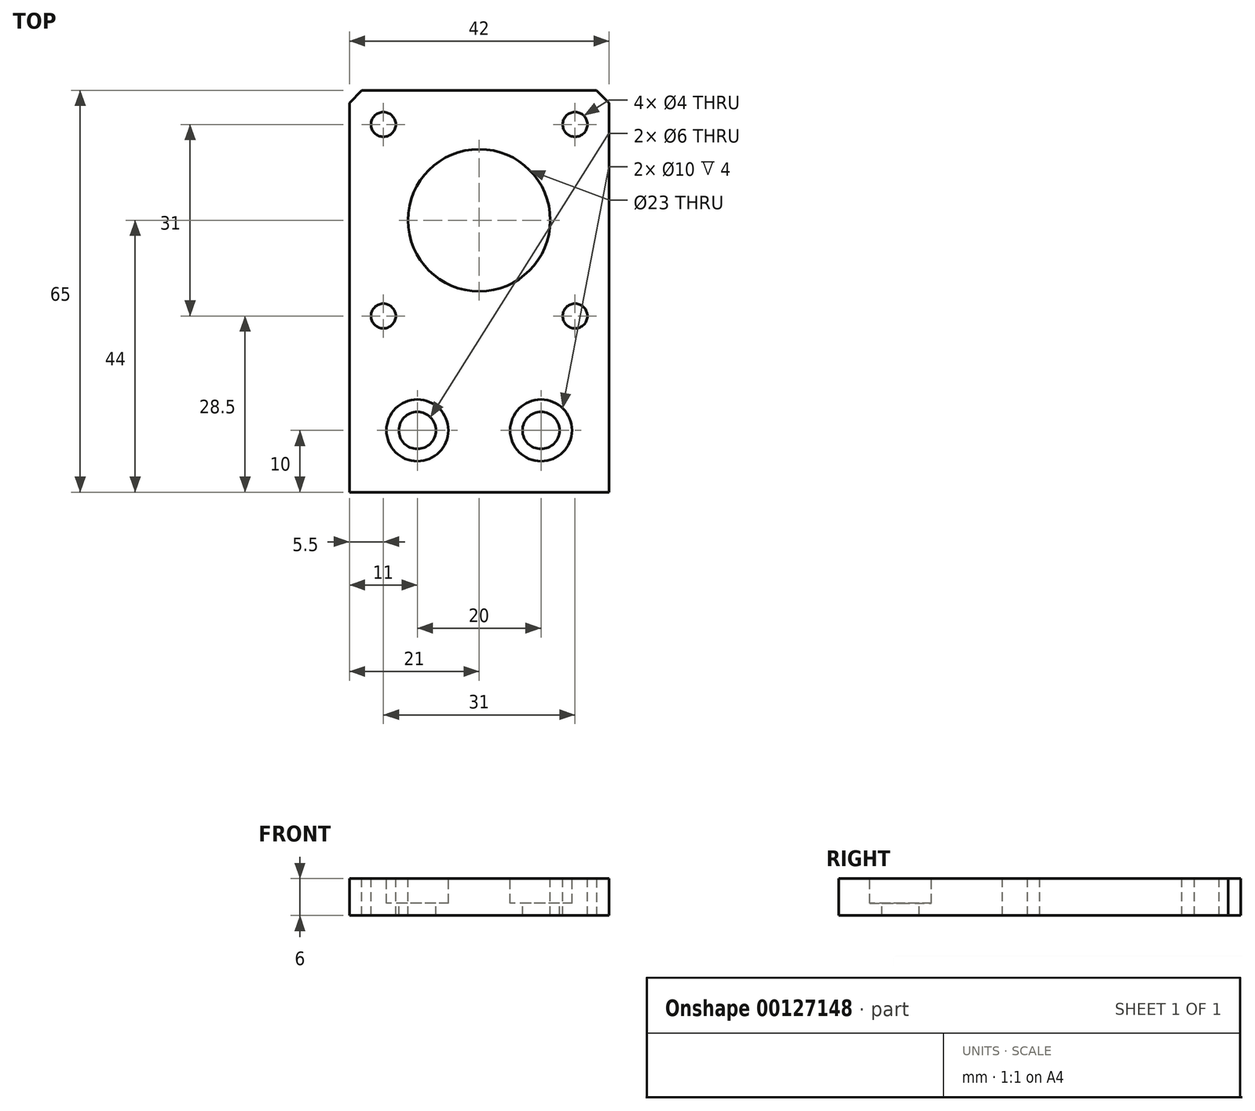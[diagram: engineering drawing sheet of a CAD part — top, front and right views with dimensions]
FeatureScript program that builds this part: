
annotation { "Feature Type Name" : "Feature", "Feature Type Description" : "" }
export const myFeature = defineFeature(function(context is Context, id is Id, definition is map)
    precondition{}
    {
        {
            var Q0;
            Q0=qCreatedBy(makeId("Top.planeOp"),FACE);
            var sketch = newSketch(context, id + "F0", { "sketchPlane" : qUnion([Q0])});
            skLineSegment(sketch, "E0.bottom", {"start": v(21, 21) * mm, "end": v(-21, 21) * mm});
            skLineSegment(sketch, "E0.top", {"start": v(21, -21) * mm, "end": v(-21, -21) * mm});
            skLineSegment(sketch, "E0.left", {"start": v(21, 21) * mm, "end": v(21, -21) * mm});
            skLineSegment(sketch, "E0.right", {"start": v(-21, 21) * mm, "end": v(-21, -21) * mm});
            skPoint(sketch, "E0.middle", {"position": v(0, 0) * mm});
            skSolve(sketch);
        }
        {
            var Q0;
            Q0=makeQuery(id+"F0.imprint","IMPRINT",FACE,{"disambiguationData":[TD([[makeQuery(id+"F0.imprint","IMPRINT",EDGE,{"derivedFrom":sQuery(id+"F0.wireOp",EDGE,"E0.bottom")}),1.0]])]});
            extrude(context, id + "F1", {"entities" : qUnion([Q0]), "depth" : 4 * mm});
        }
        {
            var Q0;
            Q0=makeQuery(id+"F1.opExtrude","CAP_FACE",FACE,{"disambiguationData":[OSD([sQuery(id+"F0.wireOp",EDGE,"E0.bottom"),sQuery(id+"F0.wireOp",EDGE,"E0.top"),sQuery(id+"F0.wireOp",EDGE,"E0.left"),sQuery(id+"F0.wireOp",EDGE,"E0.right")])],"isStart":false});
            var sketch = newSketch(context, id + "F2", { "sketchPlane" : qUnion([Q0])});
            skPoint(sketch, "E1", {"position": v(0, 0) * mm});
            skLineSegment(sketch, "E2.bottom", {"start": v(15.5, 15.5) * mm, "end": v(-15.5, 15.5) * mm});
            skLineSegment(sketch, "E2.top", {"start": v(15.5, -15.5) * mm, "end": v(-15.5, -15.5) * mm});
            skLineSegment(sketch, "E2.left", {"start": v(15.5, 15.5) * mm, "end": v(15.5, -15.5) * mm});
            skLineSegment(sketch, "E2.right", {"start": v(-15.5, 15.5) * mm, "end": v(-15.5, -15.5) * mm});
            skSolve(sketch);
        }
        {
            var Q0;
            Q0=sQuery(id+"F2.wireOp",VERTEX,"E2.right.start");
            var Q1;
            Q1=sQuery(id+"F2.wireOp",VERTEX,"E2.top.end");
            var Q2;
            Q2=sQuery(id+"F2.wireOp",VERTEX,"E2.left.start");
            var Q3;
            Q3=sQuery(id+"F2.wireOp",VERTEX,"E2.left.end");
            var Q4;
            Q4=makeQuery(id+"F1.opExtrude","SWEPT_BODY",BODY,{"disambiguationData":[OSD([sQuery(id+"F0.wireOp",EDGE,"E0.bottom"),sQuery(id+"F0.wireOp",EDGE,"E0.top"),sQuery(id+"F0.wireOp",EDGE,"E0.left"),sQuery(id+"F0.wireOp",EDGE,"E0.right")])]});
            hole(context, id + "F3", {"style" : HoleStyle.SIMPLE, "endStyle" : HoleEndStyle.BLIND, "holeDiameter" : 4 * mm, "holeDepth" : 55 * mm, "locations" : qUnion([Q0, Q1, Q2, Q3]), "scope" : qUnion([Q4])});
        }
        {
            var Q0;
            Q0=sQuery(id+"F2.wireOp",VERTEX,"E1");
            var Q1;
            Q1=makeQuery(id+"F1.opExtrude","SWEPT_BODY",BODY,{"disambiguationData":[OSD([sQuery(id+"F0.wireOp",EDGE,"E0.bottom"),sQuery(id+"F0.wireOp",EDGE,"E0.top"),sQuery(id+"F0.wireOp",EDGE,"E0.left"),sQuery(id+"F0.wireOp",EDGE,"E0.right")])]});
            hole(context, id + "F4", {"style" : HoleStyle.SIMPLE, "endStyle" : HoleEndStyle.BLIND, "holeDiameter" : 23 * mm, "holeDepth" : 55 * mm, "locations" : qUnion([Q0]), "scope" : qUnion([Q1])});
        }
        {
            var Q0;
            Q0=makeQuery(id+"F1.opExtrude","SWEPT_FACE",FACE,{"disambiguationData":[OSD([sQuery(id+"F0.wireOp",EDGE,"E0.top")])]});
            extrude(context, id + "F5", {"entities" : qUnion([Q0]), "operationType" : NewBodyOperationType.ADD, "depth" : 23 * mm});
        }
        {
            var Q0;
            {var subQ0=sQuery(id+"F0.wireOp",EDGE,"E0.top");Q0=makeQuery(id+"F5.boolean.opBoolean","MERGE",FACE,{"derivedFrom":[makeQuery(id+"F1.opExtrude","CAP_FACE",FACE,{"disambiguationData":[OSD([sQuery(id+"F0.wireOp",EDGE,"E0.bottom"),subQ0,sQuery(id+"F0.wireOp",EDGE,"E0.left"),sQuery(id+"F0.wireOp",EDGE,"E0.right")])],"isStart":false}),makeQuery(id+"F5.opExtrude","SWEPT_FACE",FACE,{"disambiguationData":[OSD([subQ0]),TDD([makeQuery(id+"F1.opExtrude","CAP_EDGE",EDGE,{"disambiguationData":[OSD([subQ0])],"isStart":false})])]})]});}
            var sketch = newSketch(context, id + "F6", { "sketchPlane" : qUnion([Q0])});
            skPoint(sketch, "E3", {"position": v(-10, -34) * mm});
            skPoint(sketch, "E4", {"position": v(10, -34) * mm});
            skSolve(sketch);
        }
        {
            var Q0;
            Q0=sQuery(id+"F6.wireOp",VERTEX,"E3");
            var Q1;
            Q1=sQuery(id+"F6.wireOp",VERTEX,"E4");
            var Q2;
            Q2=makeQuery(id+"F1.opExtrude","SWEPT_BODY",BODY,{"disambiguationData":[OSD([sQuery(id+"F0.wireOp",EDGE,"E0.bottom"),sQuery(id+"F0.wireOp",EDGE,"E0.top"),sQuery(id+"F0.wireOp",EDGE,"E0.left"),sQuery(id+"F0.wireOp",EDGE,"E0.right")])]});
            hole(context, id + "F7", {"style" : HoleStyle.C_BORE, "endStyle" : HoleEndStyle.BLIND, "holeDiameter" : 6 * mm, "cBoreDiameter" : 10 * mm, "cBoreDepth" : 2 * mm, "holeDepth" : 55 * mm, "locations" : qUnion([Q0, Q1]), "scope" : qUnion([Q2])});
        }
        {
            var Q0;
            Q0=makeQuery(id+"F1.opExtrude","SWEPT_EDGE",EDGE,{"disambiguationData":[OSD([sQuery(id+"F0.wireOp",EDGE,"E0.bottom"),sQuery(id+"F0.wireOp",EDGE,"E0.left")])]});
            var Q1;
            Q1=makeQuery(id+"F1.opExtrude","SWEPT_EDGE",EDGE,{"disambiguationData":[OSD([sQuery(id+"F0.wireOp",EDGE,"E0.bottom"),sQuery(id+"F0.wireOp",EDGE,"E0.right")])]});
            chamfer(context, id + "F8", {"entities" : qUnion([Q0, Q1]), "width" : 2 * mm, "tangentPropagation" : true});
        }
        {
            var Q0;
            {var subQ0=sQuery(id+"F0.wireOp",EDGE,"E0.top");Q0=makeQuery(id+"F5.boolean.opBoolean","MERGE",FACE,{"derivedFrom":[makeQuery(id+"F1.opExtrude","CAP_FACE",FACE,{"disambiguationData":[OSD([sQuery(id+"F0.wireOp",EDGE,"E0.bottom"),subQ0,sQuery(id+"F0.wireOp",EDGE,"E0.left"),sQuery(id+"F0.wireOp",EDGE,"E0.right")])],"isStart":false}),makeQuery(id+"F5.opExtrude","SWEPT_FACE",FACE,{"disambiguationData":[OSD([subQ0]),TDD([makeQuery(id+"F1.opExtrude","CAP_EDGE",EDGE,{"disambiguationData":[OSD([subQ0])],"isStart":false})])]})]});}
            extrude(context, id + "F9", {"entities" : qUnion([Q0]), "operationType" : NewBodyOperationType.ADD, "depth" : 2 * mm});
        }
    });
